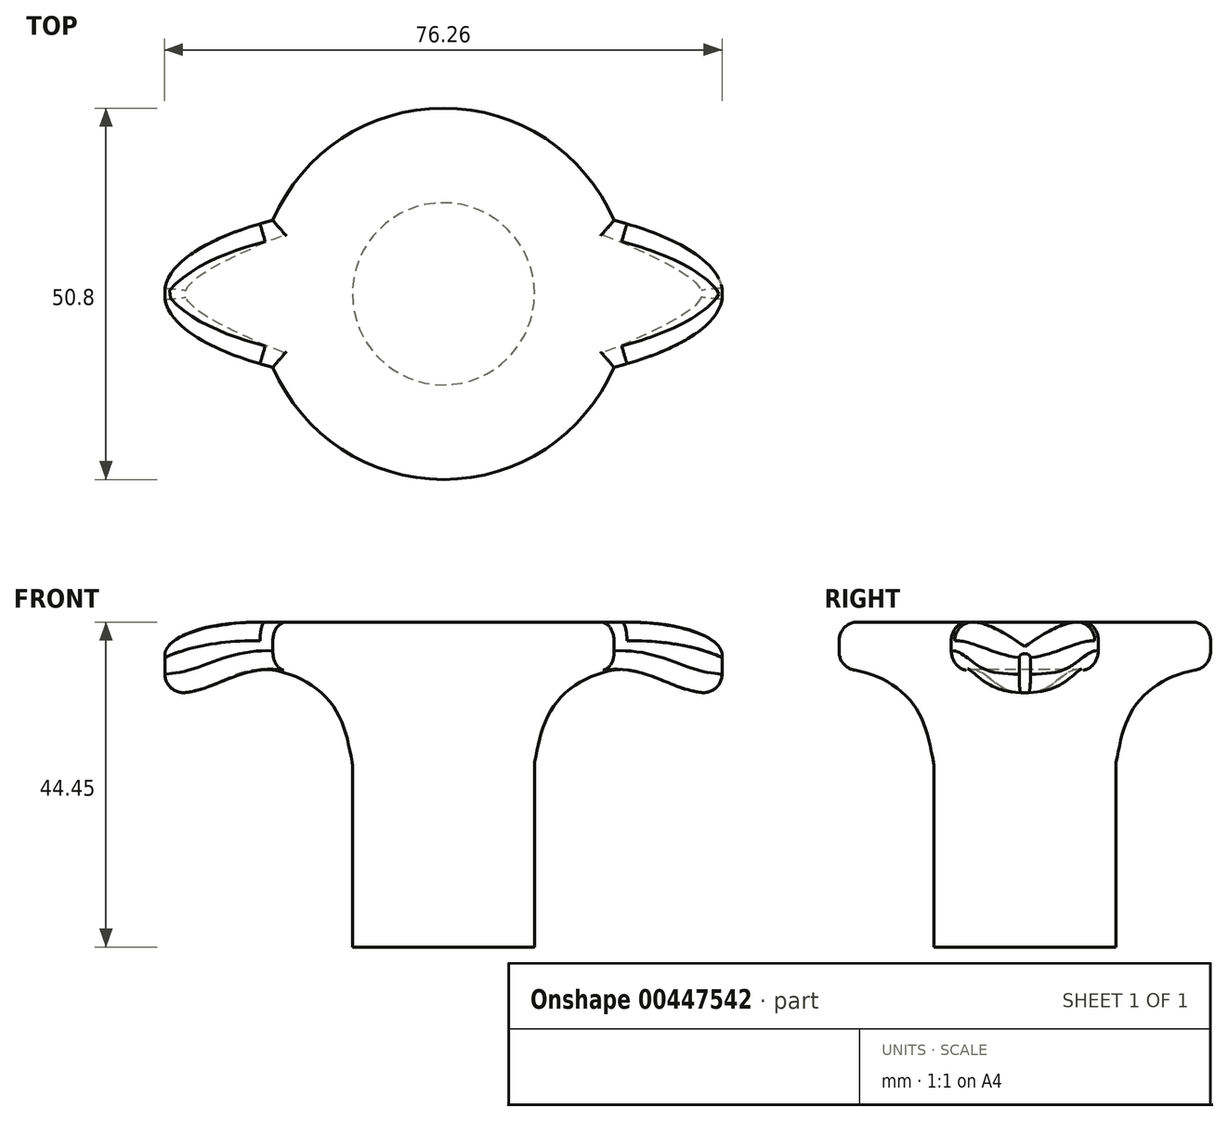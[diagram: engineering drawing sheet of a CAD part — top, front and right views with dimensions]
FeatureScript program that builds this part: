
annotation { "Feature Type Name" : "Feature", "Feature Type Description" : "" }
export const myFeature = defineFeature(function(context is Context, id is Id, definition is map)
    precondition{}
    {
        {
            var Q0;
            Q0=qCreatedBy(makeId("Front.planeOp"),FACE);
            var sketch = newSketch(context, id + "F0", { "sketchPlane" : qUnion([Q0])});
            skLineSegment(sketch, "E0", {"start": v(0, 0) * mm, "end": v(-12.45, 0) * mm});
            skLineSegment(sketch, "E1", {"start": v(0, 0) * mm, "end": v(0, 25.4) * mm, "construction": true});
            skLineSegment(sketch, "E2", {"start": v(0, 25.4) * mm, "end": v(-25.4, 25.4) * mm});
            skLineSegment(sketch, "E3", {"start": v(-12.45, 0) * mm, "end": v(-12.45, 6) * mm});
            skLineSegment(sketch, "E4", {"start": v(0, 25.4) * mm, "end": v(0, 0) * mm});
            skLineSegment(sketch, "E5", {"start": v(-12.45, 6) * mm, "end": v(-25.14, 6.23) * mm, "construction": true});
            skLineSegment(sketch, "E6", {"start": v(-25.14, 6.23) * mm, "end": v(-44.2, 6.23) * mm, "construction": true});
            skLineSegment(sketch, "E7", {"start": v(0, 0) * mm, "end": v(0, -19.05) * mm});
            skLineSegment(sketch, "E8", {"start": v(-12.45, 0) * mm, "end": v(-12.45, -19.05) * mm});
            skLineSegment(sketch, "E9", {"start": v(0, -19.05) * mm, "end": v(-12.45, -19.05) * mm});
            skArc(sketch, "E10", {"start": v(-12.45, 6) * mm, "mid": v(-25.03, 18.93) * mm, "end": v(-37.84, 6.23) * mm, "construction": true});
            skLineSegment(sketch, "E11", {"start": v(-25.4, 25.4) * mm, "end": v(-38.35, 25.4) * mm, "construction": true});
            skLineSegment(sketch, "E12", {"start": v(-38.35, 25.4) * mm, "end": v(-38.35, 19.05) * mm, "construction": true});
            skLineSegment(sketch, "E13", {"start": v(-38.35, 19.05) * mm, "end": v(-32, 19.05) * mm, "construction": true});
            skArc(sketch, "E14", {"start": v(-31.88, 25.4) * mm, "mid": v(-38.35, 19.11) * mm, "end": v(-32, 12.7) * mm, "construction": true});
            skPoint(sketch, "E15.2.internal.snap0", {"position": v(-25.03, 18.93) * mm});
            skPoint(sketch, "E16.6.internal.snap0", {"position": v(-38.35, 22.23) * mm});
            skFitSpline(sketch, "E16", {"points": [v(-12.45, 6) * mm, v(-15.71, 14.74) * mm, v(-25.03, 18.93) * mm, v(-32.8, 16.37) * mm, v(-37.66, 16.15) * mm, v(-38.35, 19.05) * mm, v(-37.5, 22.23) * mm, v(-25.4, 25.4) * mm], "startDerivative": vector(-10.5, 56.51) * mm, "endDerivative": vector(92.08, 0) * mm});
            skSolve(sketch);
        }
        {
            var Q0;
            Q0=makeQuery(id+"F0.imprint","IMPRINT",FACE,{"disambiguationData":[TD([[makeQuery(id+"F0.imprint","IMPRINT",EDGE,{"derivedFrom":sQuery(id+"F0.wireOp",EDGE,"E0")}),-1.0]])]});
            var Q1;
            Q1=makeQuery(id+"F0.imprint","IMPRINT",FACE,{"disambiguationData":[TD([[makeQuery(id+"F0.imprint","IMPRINT",EDGE,{"derivedFrom":sQuery(id+"F0.wireOp",EDGE,"E0")}),1.0]])]});
            var Q2;
            Q2=sQuery(id+"F0.wireOp",EDGE,"E4");
            revolve(context, id + "F1", {"entities" : qUnion([Q0, Q1]), "axis" : qUnion([Q2]), "revolveType" : RevolveType.FULL});
        }
        {
            var Q0;
            Q0=qCreatedBy(makeId("Top.planeOp"),FACE);
            var sketch = newSketch(context, id + "F2", { "sketchPlane" : qUnion([Q0])});
            skLineSegment(sketch, "E17", {"start": v(0, 0) * mm, "end": v(0, 12.7) * mm, "construction": true});
            skLineSegment(sketch, "E18", {"start": v(0, 0) * mm, "end": v(-38.16, 0) * mm, "construction": true});
            skArc(sketch, "E19", {"start": v(-23.33, -10.05) * mm, "mid": v(0, -25.4) * mm, "end": v(23.33, -10.05) * mm});
            skCircle(sketch, "E20", {"center": v(0, 0) * mm, "radius": 38.1 * mm});
            skEllipticalArc(sketch, "E21", {});
            skEllipticalArc(sketch, "E22.trimOffspring", {});
            skArc(sketch, "E23.trimOffspring", {"start": v(23.33, 10.05) * mm, "mid": v(0, 25.4) * mm, "end": v(-23.33, 10.05) * mm});
            const initialGuessF2  = {"E21": [0, 0, -1, 0, 0.03816171337043263, 0.0127, 5.370038988073175, 0.9131463191064109], "E22.trimOffspring": [0, 0, -1, 0, 0.03816171337043263, 0.0127, 2.228446334483383, 4.054738972696203]};
            skSetInitialGuess(sketch, initialGuessF2);
            skSolve(sketch);
        }
        {
            var Q0;
            {var subQ7=sQuery(id+"F2.wireOp",EDGE,"E19");Q0=makeQuery(id+"F2.imprint","IMPRINT",FACE,{"disambiguationData":[TD([[makeQuery(id+"F2.imprint","IMPRINT",EDGE,{"derivedFrom":subQ7}),1.0]])]});}
            extrude(context, id + "F3", {"entities" : qUnion([Q0]), "operationType" : NewBodyOperationType.INTERSECT, "depth" : 76.2 * mm, "hasSecondDirection" : true, "secondDirectionOppositeDirection" : true, "secondDirectionDepth" : 54.36 * mm});
        }
        {
            var Q0;
            {var subQ0=sQuery(id+"F2.wireOp",EDGE,"E21");var subQ1=sQuery(id+"F2.wireOp",EDGE,"E20");var subQ2=makeQuery(id+"F2.imprint","INTERSECT",VERTEX,{"disambiguationData":[OD(0.0)],"derivedFrom":[subQ1,subQ0]});var subQ4=sQuery(id+"F2.wireOp",EDGE,"E19");var subQ5=sQuery(id+"F2.wireOp",EDGE,"E23.trimOffspring");Q0=makeQuery(id+"F3.boolean.opBoolean","SPLIT",FACE,{"disambiguationData":[TD([makeQuery(id+"F1.opRevolve","SWEPT_FACE",FACE,{"disambiguationData":[OSD([sQuery(id+"F0.wireOp",EDGE,"E2")])]}),makeQuery(id+"F3.boolean.toolComplement.opBoolean","COPY",FACE,{"derivedFrom":makeQuery(id+"F3.opExtrude","SWEPT_FACE",FACE,{"disambiguationData":[OSD([subQ4])]})}),makeQuery(id+"F3.boolean.toolComplement.opBoolean","COPY",FACE,{"derivedFrom":makeQuery(id+"F3.opExtrude","SWEPT_FACE",FACE,{"disambiguationData":[OSD([subQ1]),TDD([makeQuery(id+"F2.imprint","IMPRINT",EDGE,{"disambiguationData":[TD([[subQ2,1.0]])],"derivedFrom":subQ1})])]})}),makeQuery(id+"F3.boolean.toolComplement.opBoolean","COPY",FACE,{"derivedFrom":makeQuery(id+"F3.opExtrude","SWEPT_FACE",FACE,{"disambiguationData":[OSD([subQ0]),TDD([makeQuery(id+"F2.imprint","IMPRINT",EDGE,{"disambiguationData":[TD([[makeQuery(id+"F2.imprint","INTERSECT",VERTEX,{"derivedFrom":[subQ4,subQ0]}),1.0]])],"derivedFrom":subQ0})])]})}),makeQuery(id+"F3.boolean.toolComplement.opBoolean","COPY",FACE,{"derivedFrom":makeQuery(id+"F3.opExtrude","SWEPT_FACE",FACE,{"disambiguationData":[OSD([subQ0]),TDD([makeQuery(id+"F2.imprint","IMPRINT",EDGE,{"disambiguationData":[TD([[makeQuery(id+"F2.imprint","INTERSECT",VERTEX,{"derivedFrom":[subQ0,subQ5]}),-1.0]])],"derivedFrom":subQ0})])]})}),makeQuery(id+"F3.boolean.toolComplement.opBoolean","COPY",FACE,{"derivedFrom":makeQuery(id+"F3.opExtrude","SWEPT_FACE",FACE,{"disambiguationData":[OSD([subQ5])]})})])],"derivedFrom":makeQuery(id+"F1.opRevolve","SWEPT_FACE",FACE,{"disambiguationData":[OSD([sQuery(id+"F0.wireOp",EDGE,"E16")])]})});}
            var Q1;
            {var subQ0=sQuery(id+"F2.wireOp",EDGE,"E22.trimOffspring");var subQ1=sQuery(id+"F2.wireOp",EDGE,"E20");var subQ2=makeQuery(id+"F2.imprint","INTERSECT",VERTEX,{"disambiguationData":[OD(0.0)],"derivedFrom":[subQ1,subQ0]});var subQ4=sQuery(id+"F2.wireOp",EDGE,"E19");var subQ5=sQuery(id+"F2.wireOp",EDGE,"E21");var subQ6=makeQuery(id+"F2.imprint","INTERSECT",VERTEX,{"disambiguationData":[OD(0.0)],"derivedFrom":[subQ1,subQ5]});var subQ8=sQuery(id+"F2.wireOp",EDGE,"E23.trimOffspring");Q1=makeQuery(id+"F3.boolean.opBoolean","SPLIT",FACE,{"disambiguationData":[TD([makeQuery(id+"F1.opRevolve","SWEPT_FACE",FACE,{"disambiguationData":[OSD([sQuery(id+"F0.wireOp",EDGE,"E3"),sQuery(id+"F0.wireOp",EDGE,"E8")])]}),makeQuery(id+"F3.boolean.toolComplement.opBoolean","COPY",FACE,{"derivedFrom":makeQuery(id+"F3.opExtrude","SWEPT_FACE",FACE,{"disambiguationData":[OSD([subQ4])]})}),makeQuery(id+"F3.boolean.toolComplement.opBoolean","COPY",FACE,{"derivedFrom":makeQuery(id+"F3.opExtrude","SWEPT_FACE",FACE,{"disambiguationData":[OSD([subQ1]),TDD([makeQuery(id+"F2.imprint","IMPRINT",EDGE,{"disambiguationData":[TD([[subQ6,1.0]])],"derivedFrom":subQ1})])]})}),makeQuery(id+"F3.boolean.toolComplement.opBoolean","COPY",FACE,{"derivedFrom":makeQuery(id+"F3.opExtrude","SWEPT_FACE",FACE,{"disambiguationData":[OSD([subQ1]),TDD([makeQuery(id+"F2.imprint","IMPRINT",EDGE,{"disambiguationData":[TD([[subQ2,1.0]])],"derivedFrom":subQ1})])]})}),makeQuery(id+"F3.boolean.toolComplement.opBoolean","COPY",FACE,{"derivedFrom":makeQuery(id+"F3.opExtrude","SWEPT_FACE",FACE,{"disambiguationData":[OSD([subQ5]),TDD([makeQuery(id+"F2.imprint","IMPRINT",EDGE,{"disambiguationData":[TD([[makeQuery(id+"F2.imprint","INTERSECT",VERTEX,{"derivedFrom":[subQ4,subQ5]}),1.0]])],"derivedFrom":subQ5})])]})}),makeQuery(id+"F3.boolean.toolComplement.opBoolean","COPY",FACE,{"derivedFrom":makeQuery(id+"F3.opExtrude","SWEPT_FACE",FACE,{"disambiguationData":[OSD([subQ5]),TDD([makeQuery(id+"F2.imprint","IMPRINT",EDGE,{"disambiguationData":[TD([[makeQuery(id+"F2.imprint","INTERSECT",VERTEX,{"derivedFrom":[subQ5,subQ8]}),-1.0]])],"derivedFrom":subQ5})])]})}),makeQuery(id+"F3.boolean.toolComplement.opBoolean","COPY",FACE,{"derivedFrom":makeQuery(id+"F3.opExtrude","SWEPT_FACE",FACE,{"disambiguationData":[OSD([subQ0]),TDD([makeQuery(id+"F2.imprint","IMPRINT",EDGE,{"disambiguationData":[TD([[makeQuery(id+"F2.imprint","INTERSECT",VERTEX,{"derivedFrom":[subQ4,subQ0]}),-1.0]])],"derivedFrom":subQ0})])]})}),makeQuery(id+"F3.boolean.toolComplement.opBoolean","COPY",FACE,{"derivedFrom":makeQuery(id+"F3.opExtrude","SWEPT_FACE",FACE,{"disambiguationData":[OSD([subQ0]),TDD([makeQuery(id+"F2.imprint","IMPRINT",EDGE,{"disambiguationData":[TD([[makeQuery(id+"F2.imprint","INTERSECT",VERTEX,{"derivedFrom":[subQ0,subQ8]}),1.0]])],"derivedFrom":subQ0})])]})}),makeQuery(id+"F3.boolean.toolComplement.opBoolean","COPY",FACE,{"derivedFrom":makeQuery(id+"F3.opExtrude","SWEPT_FACE",FACE,{"disambiguationData":[OSD([subQ8])]})})])],"derivedFrom":makeQuery(id+"F1.opRevolve","SWEPT_FACE",FACE,{"disambiguationData":[OSD([sQuery(id+"F0.wireOp",EDGE,"E16")])]})});}
            var Q2;
            {var subQ0=sQuery(id+"F2.wireOp",EDGE,"E22.trimOffspring");var subQ1=sQuery(id+"F2.wireOp",EDGE,"E20");var subQ2=makeQuery(id+"F2.imprint","INTERSECT",VERTEX,{"disambiguationData":[OD(0.0)],"derivedFrom":[subQ1,subQ0]});var subQ4=sQuery(id+"F2.wireOp",EDGE,"E19");var subQ5=sQuery(id+"F2.wireOp",EDGE,"E23.trimOffspring");Q2=makeQuery(id+"F3.boolean.opBoolean","SPLIT",FACE,{"disambiguationData":[TD([makeQuery(id+"F1.opRevolve","SWEPT_FACE",FACE,{"disambiguationData":[OSD([sQuery(id+"F0.wireOp",EDGE,"E2")])]}),makeQuery(id+"F3.boolean.toolComplement.opBoolean","COPY",FACE,{"derivedFrom":makeQuery(id+"F3.opExtrude","SWEPT_FACE",FACE,{"disambiguationData":[OSD([subQ4])]})}),makeQuery(id+"F3.boolean.toolComplement.opBoolean","COPY",FACE,{"derivedFrom":makeQuery(id+"F3.opExtrude","SWEPT_FACE",FACE,{"disambiguationData":[OSD([subQ1]),TDD([makeQuery(id+"F2.imprint","IMPRINT",EDGE,{"disambiguationData":[TD([[subQ2,1.0]])],"derivedFrom":subQ1})])]})}),makeQuery(id+"F3.boolean.toolComplement.opBoolean","COPY",FACE,{"derivedFrom":makeQuery(id+"F3.opExtrude","SWEPT_FACE",FACE,{"disambiguationData":[OSD([subQ0]),TDD([makeQuery(id+"F2.imprint","IMPRINT",EDGE,{"disambiguationData":[TD([[makeQuery(id+"F2.imprint","INTERSECT",VERTEX,{"derivedFrom":[subQ4,subQ0]}),-1.0]])],"derivedFrom":subQ0})])]})}),makeQuery(id+"F3.boolean.toolComplement.opBoolean","COPY",FACE,{"derivedFrom":makeQuery(id+"F3.opExtrude","SWEPT_FACE",FACE,{"disambiguationData":[OSD([subQ0]),TDD([makeQuery(id+"F2.imprint","IMPRINT",EDGE,{"disambiguationData":[TD([[makeQuery(id+"F2.imprint","INTERSECT",VERTEX,{"derivedFrom":[subQ0,subQ5]}),1.0]])],"derivedFrom":subQ0})])]})}),makeQuery(id+"F3.boolean.toolComplement.opBoolean","COPY",FACE,{"derivedFrom":makeQuery(id+"F3.opExtrude","SWEPT_FACE",FACE,{"disambiguationData":[OSD([subQ5])]})})])],"derivedFrom":makeQuery(id+"F1.opRevolve","SWEPT_FACE",FACE,{"disambiguationData":[OSD([sQuery(id+"F0.wireOp",EDGE,"E16")])]})});}
            var Q3;
            Q3=makeQuery(id+"F1.opRevolve","SWEPT_FACE",FACE,{"disambiguationData":[OSD([sQuery(id+"F0.wireOp",EDGE,"E2")])]});
            fillet(context, id + "F4", {"entities" : qUnion([Q0, Q1, Q2, Q3]), "radius" : 2.54 * mm, "tangentPropagation" : true, "allowEdgeOverflow" : false});
        }
    });
